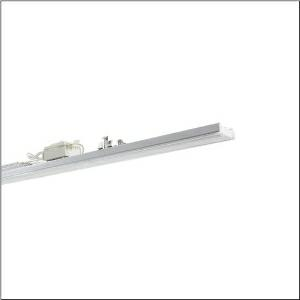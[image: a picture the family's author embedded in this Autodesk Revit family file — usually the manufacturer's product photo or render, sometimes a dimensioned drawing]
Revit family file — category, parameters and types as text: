
# Revit family: licross_21_recessed_ho_52tl12dn4fxm3s
name_source: partatom
category: Lighting Fixtures
units: mm (PartAtom-declared; Revit-internal decimal feet)

## family parameters
Cut with Voids When Loaded = No
Host = Face
Light Source = No
Part Type = Normal
Room Calculation Point = No
Round Connector Dimension = Use Diameter
Shared = No

## types (1)
- --- (1 x LED, 930 lm, 7.5 W, 4000K)
    Apparent Load = 8 VA
    CIE Flux Codes = 69 91 98 100 100
    Color Rendering = 80
    Color Temperature = 4000K
    Default Elevation = 1800 mm
    Description = Licross 21 Recessed HO, luminaire insert, of sheet steel, galvanised, coil coated, white, length: 1.500mm, width: 66mm, height: 67mm, LED rated luminous flux: 15.000lm, light colour: 840, SDCM (Standard Deviation of Colour Matching)MacAdam ≤ 3 SDCM (initial), control gear: DALI 2 (for two DALI lines), with plug, 6-pole, with phase selection, for trunking rail, 14-core, mains connection: 220..240V, AC, 50/60Hz, rated input power: 88W, internal wiring halogen-free, for emergency light function, for trunking rail, 14-core, converter,control gear: single battery element, battery: LiFePO4, 9Ah, primary optical cover: cover, of PMMA, light emission: direct distribution, primary light characteristic: symmetric, protection rating (complete): IP40, insulation class (complete): insulation class I (protective earthing), certification: CE, UKCA, protection symbol: D if used in an environment without relevant dust loads with corresponding accessories, impact resistance: IK06, permissible ambient temperature for indoor applications: +5..+30°C, standard: EN 60598-2-22, LABS conformity tested according to VDMA 24364:2018-05, reducing of maximum allowable ambient temperature of 5°C with ceiling mounting, corresponds to IFS (International Featured Standards) requirements for safety and quality in the food industry, The light source and the operating device comply with the requirements of the Ecodesign Regulation (EU) 2019/2020 and are replaceable in accordance with this regulation, packaging unit: 1 piece
    Height = 58 mm
    Lamp = 1 x LED
    Lamp Light Flux = 930 lm
    Lamp Power = 7.5 W
    Lamp count = 1
    Length = 1500 mm
    Luminous efficacy = 124 lm/W
    Manufacturer = Siteco
    ModVariant = No
    Model = 52TL12DN4FXM3S
    Mounting Place = Ceiling
    Mounting Type = Pendant
    Number of Poles = 1
    OnlyDefault = Yes
    Power Factor = 1
    Product Name = Licross 21 Recessed HO
    Product group = luminaire insert | ceiling pendant
    ProductGroupID = 901
    Protection Class = Protection class I
    Protection Degree = IP 40
    RLX_Detail_Level = 1
    RLX_Emergency_Light_Flux = 0 lm
    RLX_Emergency_Type = 0
    RLX_Emergency_Type_DB = No
    RlxData = <blob elided: 25365 chars, md5=f4d42c9d>
    Socket = socket
    Standby Power = 0 W
    System Light Flux = 930 lm
    System Power = 8 W
    Type Comments = : emergency light operation: 3 h
    Type Image = l_1296930.jpg
    URL = http://relux.com
    VarID = @adj_109227
    Voltage = 0 V
    Weight = 0.00 kg
    Width = 66 mm

## geometry (parser evidence)
native form markers: Blend x4, Sweep x9
no freeform markers — native parametric forms only
